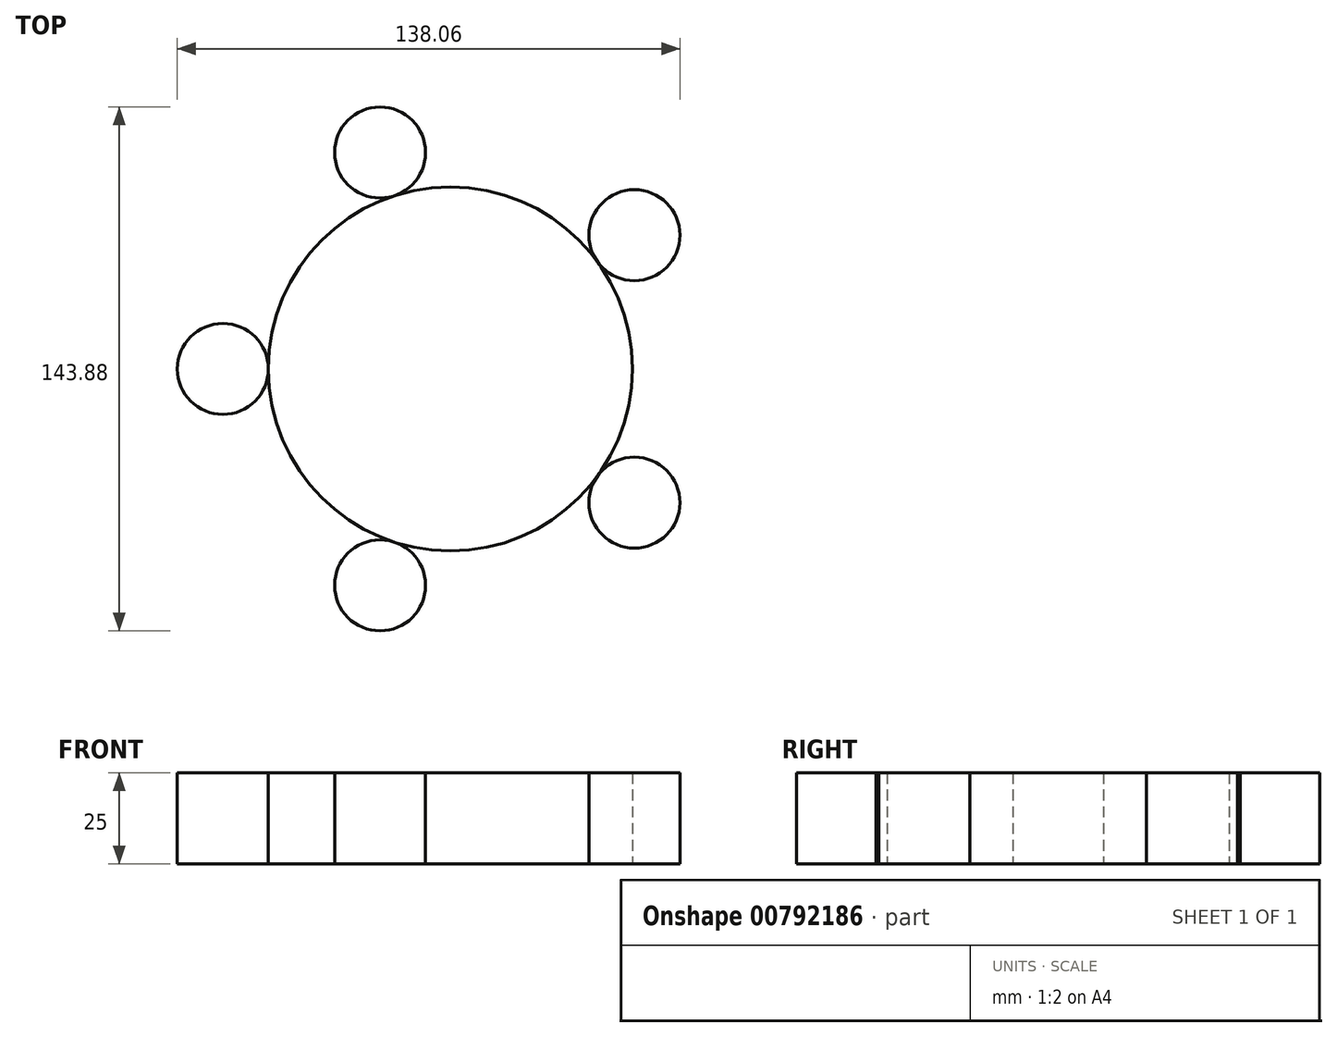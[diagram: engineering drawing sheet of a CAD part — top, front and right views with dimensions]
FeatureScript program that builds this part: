
annotation { "Feature Type Name" : "Feature", "Feature Type Description" : "" }
export const myFeature = defineFeature(function(context is Context, id is Id, definition is map)
    precondition{}
    {
        {
            var Q0;
            Q0=qCreatedBy(makeId("Top.planeOp"),FACE);
            var sketch = newSketch(context, id + "F0", { "sketchPlane" : qUnion([Q0])});
            skCircle(sketch, "E0", {"center": v(0, 0) * mm, "radius": 50 * mm});
            skCircle(sketch, "E1", {"center": v(-62.5, 0) * mm, "radius": 12.5 * mm});
            skSolve(sketch);
        }
        {
            var Q0;
            Q0=makeQuery(id+"F0.imprint","IMPRINT",FACE,{"disambiguationData":[TD([[makeQuery(id+"F0.imprint","IMPRINT",EDGE,{"derivedFrom":sQuery(id+"F0.wireOp",EDGE,"E0")}),1.0]])]});
            extrude(context, id + "F1", {"entities" : qUnion([Q0]), "depth" : 25 * mm, "offsetDistance" : 25 * mm});
        }
        {
            var Q0;
            Q0=makeQuery(id+"F0.imprint","IMPRINT",FACE,{"disambiguationData":[TD([[makeQuery(id+"F0.imprint","IMPRINT",EDGE,{"derivedFrom":sQuery(id+"F0.wireOp",EDGE,"E1")}),1.0]])]});
            extrude(context, id + "F2", {"entities" : qUnion([Q0]), "operationType" : NewBodyOperationType.ADD, "depth" : 25 * mm, "offsetDistance" : 25 * mm});
        }
        {
            var Q0;
            Q0=makeQuery(id+"F2.opExtrude","SWEPT_BODY",BODY,{"disambiguationData":[OSD([sQuery(id+"F0.wireOp",EDGE,"E1")])]});
            var Q1;
            Q1=makeQuery(id+"F1.opExtrude","CAP_EDGE",EDGE,{"disambiguationData":[OSD([sQuery(id+"F0.wireOp",EDGE,"E0")])],"isStart":false});
            circularPattern(context, id + "F3", {"entities" : qUnion([Q0]), "axis" : qUnion([Q1]), "angle" : 360 * degree, "instanceCount" : 5, "equalSpace" : true});
        }
    });
